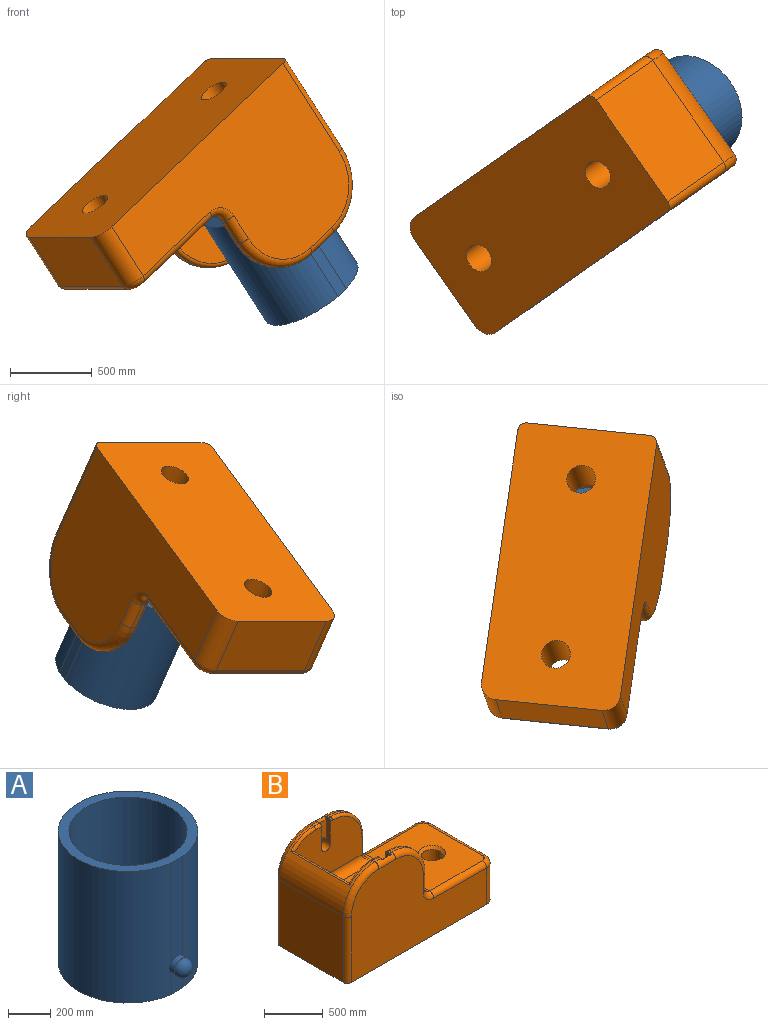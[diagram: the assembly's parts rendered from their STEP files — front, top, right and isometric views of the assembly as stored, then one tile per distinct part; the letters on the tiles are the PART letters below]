
ASSEMBLY  parts=2 mates=1
PART A: 16 faces, bbox 660.4x812.2x762 mm
  f0: cylinder r=330.2mm len=762mm, axis (0,0,-1), area 731091.1mm2, adj f2,f3,f4,f5,f8,f9,f10,f11
  f1: cylinder r=330.2mm len=762mm, axis (0,0,-1), area 731091.1mm2, adj f2,f3,f4,f5,f8,f9,f10,f11
  f2: plane 118.8x76.2mm, normal (0,-1,0), area 8144.1mm2, adj f0,f1,f5,f11
  f3: plane 118.8x76.2mm, normal (0,1,0), area 8144.1mm2, adj f0,f1,f5,f10
  f4: plane 660.4x655.99mm, normal (0,0,1), area 97063.6mm2, adj f0,f1,f6,f8,f9
  f5: plane 660.4x655.99mm, normal (0,0,-1), area 342310mm2, adj f0,f1,f2,f3
  f6: cylinder r=279.4mm len=711.2mm, axis (0,0,1), area 1248527.2mm2, adj f4,f7
  f7: plane 558.8x558.8mm, normal (0,0,1), area 245246.4mm2, adj f6
  f8: plane 576x76.2mm, normal (0,1,0), area 42982.8mm2, adj f0,f1,f4,f10
  f9: plane 576x76.2mm, normal (0,-1,0), area 42982.8mm2, adj f0,f1,f4,f11
  f10: cylinder r=50.8mm len=101.6mm, axis (0,-1,0), area 9080.6mm2, adj f0,f1,f3,f8,f13
  f11: cylinder r=50.8mm len=101.6mm, axis (0,1,0), area 10296.7mm2, adj f0,f1,f2,f9,f15
  f12: plane 5.08x5.08mm, normal (0,1,0), area 20.3mm2, adj f13
  f13: torus R=2.54mm, axis (0,1,0), area 15843.5mm2, adj f10,f12
  f14: plane 5.08x5.08mm, normal (0,-1,0), area 20.3mm2, adj f15
  f15: torus R=2.54mm, axis (0,-1,0), area 15843.5mm2, adj f11,f14
PART B: 120 faces, bbox 1817.8x880.4x1098.2 mm
  f0: plane 1778x863.6mm, normal (0,0,-1), area 1480285.4mm2, adj f9,f10,f11,f12,f41,f42,f43,f44
  f1: cone r=63.5mm half-angle=45deg, axis (0,0,1), area 22931mm2, adj f8,f61
  f2: cone r=63.5mm half-angle=45deg, axis (0,0,1), area 22931mm2, adj f8,f60
  f3: plane 25.4x25.4mm, normal (0,0,1), area 645.2mm2, adj f16,f24,f48,f66
  f4: plane 71.12x25.4mm, normal (0,0,1), area 1806.4mm2, adj f17,f28,f47,f71
  f5: plane 889x533.4mm, normal (0,1,0), area 391925.9mm2, adj f27,f28,f30,f33,f34,f35,f38,f62
  f6: plane 25.4x25.4mm, normal (0,0,1), area 645.2mm2, adj f18,f27,f47,f62
  f7: plane 71.12x25.4mm, normal (0,0,1), area 1806.4mm2, adj f17,f23,f48,f73
  f8: plane 1600.2x762mm, normal (0,0,1), area 903900.6mm2, adj f1,f2,f36,f37,f38,f39,f40,f55
  f9: plane 762x685.8mm, normal (-1,0,0), area 522579.6mm2, adj f0,f17,f43,f44
  f10: plane 1625.6x1016mm, normal (0,-1,0), area 1124404mm2, adj f0,f41,f43,f45,f47,f49,f51,f53
  f11: plane 660.4x381mm, normal (1,0,0), area 251612.4mm2, adj f0,f41,f42,f59
  f12: plane 1625.6x1016mm, normal (0,1,0), area 1124404mm2, adj f0,f42,f44,f46,f48,f50,f52,f54
  f13: plane 177.8x25.4mm, normal (1,0,0), area 4516.1mm2, adj f18,f36,f51,f64
  f14: plane 889x533.4mm, normal (0,-1,0), area 393258.3mm2, adj f21,f23,f24,f33,f34,f35,f39,f66
  f15: plane 177.8x25.4mm, normal (1,0,0), area 4516.1mm2, adj f16,f37,f52,f68
  f16: cylinder r=381mm len=381mm, axis (0,-1,0), area 15201.2mm2, adj f3,f15,f50,f67
  f17: cylinder r=381mm len=762mm, axis (0,1,0), area 234220.6mm2, adj f4,f7,f9,f45,f46,f70,f72,f75
  f18: cylinder r=381mm len=381mm, axis (0,-1,0), area 15201.2mm2, adj f6,f13,f49,f63
  f19: cylinder r=53.34mm len=106.68mm, axis (0,1,0), area 12769mm2, adj f20,f29,f31
  f20: plane 106.68x106.68mm, normal (0,1,0), area 8938.3mm2, adj f19
  f21: cylinder r=53.34mm len=106.68mm, axis (0,-1,0), area 21281.7mm2, adj f14,f22,f23,f24,f25
  f22: plane 106.68x106.68mm, normal (0,-1,0), area 8938.3mm2, adj f21
  f23: plane 254x71.7mm, normal (1,0,0), area 13046.4mm2, adj f7,f14,f21,f25,f26,f48,f73
  f24: plane 254x71.7mm, normal (-1,0,0), area 13046.4mm2, adj f3,f14,f21,f25,f26,f48,f66
  f25: plane 228.6x106.68mm, normal (0,-1,0), area 19917.9mm2, adj f21,f23,f24,f26
  f26: plane 106.68x20.9mm, normal (0,-0.71,0.71), area 3153.3mm2, adj f23,f24,f25,f48
  f27: plane 308.38x71.7mm, normal (-1,0,0), area 15809.1mm2, adj f5,f6,f29,f30,f31,f32,f47,f62
  f28: plane 308.38x71.7mm, normal (1,0,0), area 15809.1mm2, adj f4,f5,f29,f30,f31,f32,f47,f71
  f29: plane 228.6x106.68mm, normal (0,1,0), area 19917.9mm2, adj f19,f27,f28,f32
  f30: plane 106.68x50.8mm, normal (0,0,1), area 5419.3mm2, adj f5,f27,f28,f31
  f31: plane 106.68x54.38mm, normal (0,1,0), area 1332.4mm2, adj f19,f27,f28,f30
  f32: plane 106.68x20.9mm, normal (0,0.71,0.71), area 3153.3mm2, adj f27,f28,f29,f47
  f33: plane 660.4x177.8mm, normal (1,0,0), area 117419.1mm2, adj f5,f14,f34,f40
  f34: cylinder r=330.34mm len=660.4mm, axis (0,1,0), area 164097.2mm2, adj f5,f14,f33,f74
  f35: plane 667.59x18.65mm, normal (0.68,0,0.73), area 16779.9mm2, adj f5,f14,f70,f72,f74,f75
  f36: cylinder r=76.2mm len=127mm, axis (0,1,0), area 7459.3mm2, adj f8,f13,f53,f65
  f37: cylinder r=76.2mm len=127mm, axis (0,1,0), area 7459.3mm2, adj f8,f15,f54,f69
  f38: cylinder r=76.2mm len=990.6mm, axis (-1,0,0), area 107513.3mm2, adj f5,f8,f40,f65
  f39: cylinder r=76.2mm len=990.6mm, axis (1,0,0), area 107513.3mm2, adj f8,f14,f40,f69
  f40: cylinder r=76.2mm len=660.4mm, axis (0,1,0), area 72417.8mm2, adj f8,f33,f38,f39
  f41: cylinder r=101.6mm len=381mm, axis (0,0,-1), area 60804.9mm2, adj f0,f10,f11,f57
  f42: cylinder r=101.6mm len=381mm, axis (0,0,1), area 60804.9mm2, adj f0,f11,f12,f58
  f43: cylinder r=50.8mm len=685.8mm, axis (0,0,1), area 54724.4mm2, adj f0,f9,f10,f45
  f44: cylinder r=50.8mm len=685.8mm, axis (0,0,-1), area 54724.4mm2, adj f0,f9,f12,f46
  f45: torus R=330.2mm, axis (0,1,0), area 45442.2mm2, adj f10,f17,f43,f47
  f46: torus R=330.2mm, axis (0,1,0), area 45442.2mm2, adj f12,f17,f44,f48
  f47: cylinder r=50.8mm len=203.2mm, axis (-1,0,0), area 13916.7mm2, adj f4,f6,f10,f27,f28,f32,f45,f49
  f48: cylinder r=50.8mm len=203.2mm, axis (1,0,0), area 13916.7mm2, adj f3,f7,f12,f23,f24,f26,f46,f50
  f49: torus R=330.2mm, axis (0,1,0), area 45442.2mm2, adj f10,f18,f47,f51
  f50: torus R=330.2mm, axis (0,1,0), area 45442.2mm2, adj f12,f16,f48,f52
  f51: cylinder r=50.8mm len=177.8mm, axis (0,0,-1), area 14187.8mm2, adj f10,f13,f49,f53
  f52: cylinder r=50.8mm len=177.8mm, axis (0,0,-1), area 14187.8mm2, adj f12,f15,f50,f54
  f53: torus R=127mm, axis (0,1,0), area 11865mm2, adj f10,f36,f51,f55
  f54: torus R=127mm, axis (0,1,0), area 11865mm2, adj f12,f37,f52,f56
  f55: cylinder r=50.8mm len=635mm, axis (-1,0,0), area 50670.7mm2, adj f8,f10,f53,f57
  f56: cylinder r=50.8mm len=635mm, axis (1,0,0), area 50670.7mm2, adj f8,f12,f54,f58
  f57: torus R=50.8mm, axis (0,0,1), area 10421.1mm2, adj f8,f41,f55,f59
  f58: torus R=50.8mm, axis (0,0,1), area 10421.1mm2, adj f8,f42,f56,f59
  f59: cylinder r=50.8mm len=660.4mm, axis (0,-1,0), area 52697.6mm2, adj f8,f11,f57,f58
  f60: cylinder r=88.9mm len=406.4mm, axis (0,0,1), area 227005mm2, adj f0,f2
  f61: cylinder r=88.9mm len=406.4mm, axis (0,0,1), area 227005mm2, adj f0,f1
  f62: cylinder r=25.4mm len=25.4mm, axis (1,0,0), area 1013.4mm2, adj f5,f6,f27,f63
  f63: torus R=355.6mm, axis (0,1,0), area 23299.6mm2, adj f5,f18,f62,f64
  f64: cylinder r=25.4mm len=177.8mm, axis (0,0,1), area 7093.9mm2, adj f5,f13,f63,f65
  f65: bspline ~101.6x101.6mm, area 3449.9mm2, adj f36,f38,f64
  f66: cylinder r=25.4mm len=25.4mm, axis (-1,0,0), area 1013.4mm2, adj f3,f14,f24,f67
  f67: torus R=355.6mm, axis (0,1,0), area 23299.6mm2, adj f14,f16,f66,f68
  f68: cylinder r=25.4mm len=177.8mm, axis (0,0,1), area 7093.9mm2, adj f14,f15,f67,f69
  f69: bspline ~101.6x101.6mm, area 3449.9mm2, adj f37,f39,f68
  f70: torus R=355.6mm, axis (0,1,0), area 11761.3mm2, adj f5,f17,f35,f71,f75
  f71: cylinder r=25.4mm len=71.12mm, axis (1,0,0), area 2837.6mm2, adj f4,f5,f28,f70
  f72: torus R=355.6mm, axis (0,1,0), area 11761.3mm2, adj f14,f17,f35,f73,f75
  f73: cylinder r=25.4mm len=71.12mm, axis (-1,0,0), area 2837.6mm2, adj f7,f14,f23,f72
  f74: cylinder r=12.7mm len=660.4mm, axis (0,1,0), area 13207.6mm2, adj f5,f14,f34,f35
  f75: cylinder r=12.7mm len=711.2mm, axis (0,1,0), area 13662.4mm2, adj f17,f35,f70,f72
  f76: plane 444.5x177.8mm, normal (0,0,-1), area 39516mm2, adj f77,f78,f79
  f77: plane 444.5x381mm, normal (-0.37,-0.93,0), area 182400.4mm2, adj f76,f78,f79,f80
  f78: plane 444.5x381mm, normal (0,1,0), area 169354.5mm2, adj f76,f77,f79,f80
  f79: plane 381x177.8mm, normal (1,0,0), area 67741.8mm2, adj f76,f77,f78,f80
  f80: plane 444.5x177.8mm, normal (0,0,1), area 39516mm2, adj f77,f78,f79
  f81: plane 444.5x177.8mm, normal (0,0,-1), area 39516.1mm2, adj f82,f83,f84
  f82: plane 444.5x381mm, normal (0,1,0), area 169354.5mm2, adj f81,f83,f84,f85
  f83: plane 444.5x381mm, normal (0.37,-0.93,0), area 182400.4mm2, adj f81,f82,f84,f85
  f84: plane 381x177.8mm, normal (-1,0,0), area 67741.8mm2, adj f81,f82,f83,f85
  f85: plane 444.5x177.8mm, normal (0,0,1), area 39516.1mm2, adj f82,f83,f84
  f86: plane 443.03x176.97mm, normal (0,0,1), area 39201.2mm2, adj f88,f89,f90
  f87: plane 443.03x176.97mm, normal (0,0,-1), area 39201.2mm2, adj f88,f89,f90
  f88: plane 443.03x381mm, normal (0,-1,0), area 168793.5mm2, adj f86,f87,f89,f90
  f89: plane 443.03x381mm, normal (0.37,0.93,0), area 181762.1mm2, adj f86,f87,f88,f90
  f90: plane 381x176.97mm, normal (-1,0,0), area 67425.5mm2, adj f86,f87,f88,f89
  f91: plane 685.8x228.6mm, normal (0,0,1), area 91451.4mm2, adj f93,f94,f95,f96
  f92: plane 685.8x228.6mm, normal (0,0,-1), area 91451.4mm2, adj f93,f94,f95,f96
  f93: plane 381x114.3mm, normal (0,-1,0), area 43548.3mm2, adj f91,f92,f94,f95
  f94: plane 381x228.6mm, normal (1,0,0), area 87096.6mm2, adj f91,f92,f93,f96
  f95: plane 571.5x381mm, normal (-0.37,-0.93,0), area 234514.8mm2, adj f91,f92,f93,f96
  f96: plane 685.8x381mm, normal (0,1,0), area 261289.8mm2, adj f91,f92,f94,f95
  f97: plane 685.8x228.6mm, normal (0,0,1), area 91451.4mm2, adj f99,f100,f101,f102
  f98: plane 685.8x228.6mm, normal (0,0,-1), area 91451.4mm2, adj f99,f100,f101,f102
  f99: plane 381x114.3mm, normal (0,-1,0), area 43548.3mm2, adj f97,f98,f100,f101
  f100: plane 571.5x381mm, normal (0.37,-0.93,0), area 234514.8mm2, adj f97,f98,f99,f102
  f101: plane 381x228.6mm, normal (-1,0,0), area 87096.6mm2, adj f97,f98,f99,f102
  f102: plane 685.8x381mm, normal (0,1,0), area 261289.8mm2, adj f97,f98,f100,f101
  f103: plane 685.8x228.6mm, normal (0,0,-1), area 91362.3mm2, adj f104,f105,f106,f107
  f104: plane 381x113.52mm, normal (0,1,0), area 43251.3mm2, adj f103,f105,f106,f108
  f105: plane 381x228.6mm, normal (-1,0,0), area 87096.6mm2, adj f103,f104,f107,f108
  f106: plane 572.28x381mm, normal (0.37,0.93,0), area 234790.5mm2, adj f103,f104,f107,f108
  f107: plane 685.8x381mm, normal (0,-1,0), area 261289.8mm2, adj f103,f105,f106,f108
  f108: plane 685.8x228.6mm, normal (0,0,1), area 91362.3mm2, adj f104,f105,f106,f107
  f109: plane 685.8x228.6mm, normal (0,0,-1), area 91451.4mm2, adj f110,f111,f112,f113
  f110: plane 381x114.3mm, normal (0,1,0), area 43548.3mm2, adj f109,f111,f112,f114
  f111: plane 571.5x381mm, normal (-0.37,0.93,0), area 234514.8mm2, adj f109,f110,f113,f114
  f112: plane 381x228.6mm, normal (1,0,0), area 87096.6mm2, adj f109,f110,f113,f114
  f113: plane 685.8x381mm, normal (0,-1,0), area 261289.8mm2, adj f109,f111,f112,f114
  f114: plane 685.8x228.6mm, normal (0,0,1), area 91451.4mm2, adj f110,f111,f112,f113
  f115: plane 444.5x177.8mm, normal (0,0,1), area 39516mm2, adj f117,f118,f119
  f116: plane 444.5x177.8mm, normal (0,0,-1), area 39516mm2, adj f117,f118,f119
  f117: plane 444.5x381mm, normal (0,-1,0), area 169354.5mm2, adj f115,f116,f118,f119
  f118: plane 444.5x381mm, normal (-0.37,0.93,0), area 182400.4mm2, adj f115,f116,f117,f119
  f119: plane 381x177.8mm, normal (1,0,0), area 67741.8mm2, adj f115,f116,f117,f118
PLACE A rot(axis=(-0.3,0.95,0.1),143.8deg) t=(45.78,30.76,968.47)mm
PLACE B rot(axis=(-0.3,0.95,0.1),143.8deg) t=(-230.3,-334.95,1465.97)mm
MATE revolute A.f10 <-> B.f19  axis (-0.57,0.82,0) through (-65.65,426.89,881.26)mm
